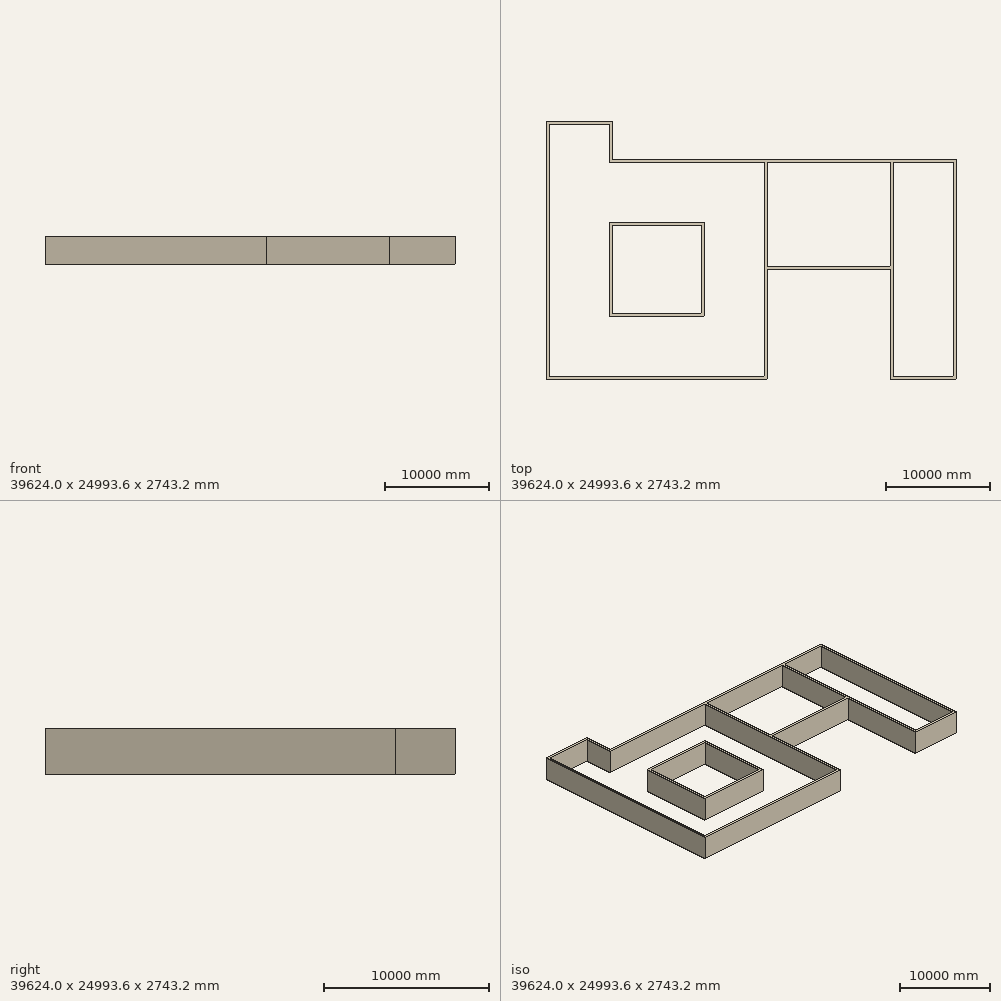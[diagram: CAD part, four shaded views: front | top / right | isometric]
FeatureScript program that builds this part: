
annotation { "Feature Type Name" : "Feature", "Feature Type Description" : "" }
export const myFeature = defineFeature(function(context is Context, id is Id, definition is map)
    precondition{}
    {
        {
            var Q0;
            Q0=qCreatedBy(makeId("Top.planeOp"),FACE);
            var sketch = newSketch(context, id + "F0", { "sketchPlane" : qUnion([Q0])});
            skLineSegment(sketch, "E0.bottom", {"start": v(0, 0) * mm, "end": v(21336, 0) * mm});
            skLineSegment(sketch, "E0.left", {"start": v(0, 0) * mm, "end": v(0, 24993.6) * mm});
            skLineSegment(sketch, "E0.right", {"start": v(21336, 0) * mm, "end": v(21336, 10668) * mm});
            skLineSegment(sketch, "E1.bottom", {"start": v(304.8, 304.8) * mm, "end": v(21031.2, 304.8) * mm});
            skLineSegment(sketch, "E1.top", {"start": v(6096, 21031.2) * mm, "end": v(21031.2, 21031.2) * mm});
            skLineSegment(sketch, "E1.left", {"start": v(304.8, 304.8) * mm, "end": v(304.8, 24688.8) * mm});
            skLineSegment(sketch, "E1.right", {"start": v(21031.2, 304.8) * mm, "end": v(21031.2, 21031.2) * mm});
            skLineSegment(sketch, "E2.right", {"start": v(33528, 21031.2) * mm, "end": v(33528, 304.8) * mm});
            skLineSegment(sketch, "E3.trimOffspring", {"start": v(21336, 10668) * mm, "end": v(33223.2, 10668) * mm});
            skLineSegment(sketch, "E4", {"start": v(21336, 21031.2) * mm, "end": v(33223.2, 21031.2) * mm});
            skLineSegment(sketch, "E5", {"start": v(33223.2, 21031.2) * mm, "end": v(33223.2, 10972.8) * mm});
            skLineSegment(sketch, "E6", {"start": v(33223.2, 10972.8) * mm, "end": v(21336, 10972.8) * mm});
            skLineSegment(sketch, "E7.trimOffspring", {"start": v(21336, 10972.8) * mm, "end": v(21336, 21031.2) * mm});
            skLineSegment(sketch, "E8", {"start": v(6400.8, 21336) * mm, "end": v(6400.8, 24993.6) * mm});
            skLineSegment(sketch, "E9", {"start": v(6400.8, 24993.6) * mm, "end": v(0, 24993.6) * mm});
            skLineSegment(sketch, "E10", {"start": v(304.8, 24688.8) * mm, "end": v(6096, 24688.8) * mm});
            skLineSegment(sketch, "E11", {"start": v(6096, 24688.8) * mm, "end": v(6096, 21031.2) * mm});
            skLineSegment(sketch, "E12.trimOffspring", {"start": v(6400.8, 21336) * mm, "end": v(39624, 21336) * mm});
            skLineSegment(sketch, "E13", {"start": v(39624, 21336) * mm, "end": v(39624, 0) * mm});
            skLineSegment(sketch, "E14", {"start": v(39624, 0) * mm, "end": v(33223.2, 0) * mm});
            skLineSegment(sketch, "E15", {"start": v(39319.2, 21031.2) * mm, "end": v(39319.2, 304.8) * mm});
            skLineSegment(sketch, "E16", {"start": v(39319.2, 304.8) * mm, "end": v(33528, 304.8) * mm});
            skLineSegment(sketch, "E17.trimOffspring", {"start": v(33223.2, 10668) * mm, "end": v(33223.2, 0) * mm});
            skLineSegment(sketch, "E18.trimOffspring", {"start": v(33528, 21031.2) * mm, "end": v(39319.2, 21031.2) * mm});
            skSolve(sketch);
        }
        {
            var Q0;
            Q0=qCreatedBy(makeId("Top.planeOp"),FACE);
            var sketch = newSketch(context, id + "F1", { "sketchPlane" : qUnion([Q0])});
            skLineSegment(sketch, "E19.bottom", {"start": v(6096, 15240) * mm, "end": v(15240, 15240) * mm});
            skLineSegment(sketch, "E19.top", {"start": v(6096, 6096) * mm, "end": v(15240, 6096) * mm});
            skLineSegment(sketch, "E19.left", {"start": v(6096, 15240) * mm, "end": v(6096, 6096) * mm});
            skLineSegment(sketch, "E19.right", {"start": v(15240, 15240) * mm, "end": v(15240, 6096) * mm});
            skLineSegment(sketch, "E20.bottom", {"start": v(6400.8, 14935.2) * mm, "end": v(14935.2, 14935.2) * mm});
            skLineSegment(sketch, "E20.top", {"start": v(6400.8, 6400.8) * mm, "end": v(14935.2, 6400.8) * mm});
            skLineSegment(sketch, "E20.left", {"start": v(6400.8, 14935.2) * mm, "end": v(6400.8, 6400.8) * mm});
            skLineSegment(sketch, "E20.right", {"start": v(14935.2, 14935.2) * mm, "end": v(14935.2, 6400.8) * mm});
            skSolve(sketch);
        }
        {
            var Q0;
            Q0 = qSketchRegion(id + "F0", true);
            extrude(context, id + "F2", {"entities" : qUnion([Q0]), "depth" : 2743.2 * mm});
        }
        {
            var Q0;
            Q0 = qSketchRegion(id + "F1", true);
            extrude(context, id + "F3", {"entities" : qUnion([Q0]), "depth" : 2743.2 * mm});
        }
    });
